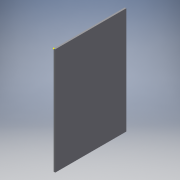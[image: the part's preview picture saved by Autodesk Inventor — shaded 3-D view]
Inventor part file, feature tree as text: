
AUTODESK INVENTOR PART (.ipt)
format: ipt  version: 2016 (Build 200138000, 138)  size: 86,016 bytes
history: native  units: in
note: dims shown in document units (in); Inventor stores cm internally (conversion verified against a paired STEP export)
features: sketch x2, extrude x1
ambient origin geometry x8: Origin, YZ Plane, XZ Plane, XY Plane, X Axis, Y Axis, Z Axis, Center Point
bodies: Solid1 (feature_tree)
feature tree (3):
  sketch  "Sketch1"  dims[d0=3.33in d1=5.0in]
  extrude  "Extrusion1"  Depth=5.0in
  sketch  "Sketch2"  dims[d2=0.071in d3=0.0in]
